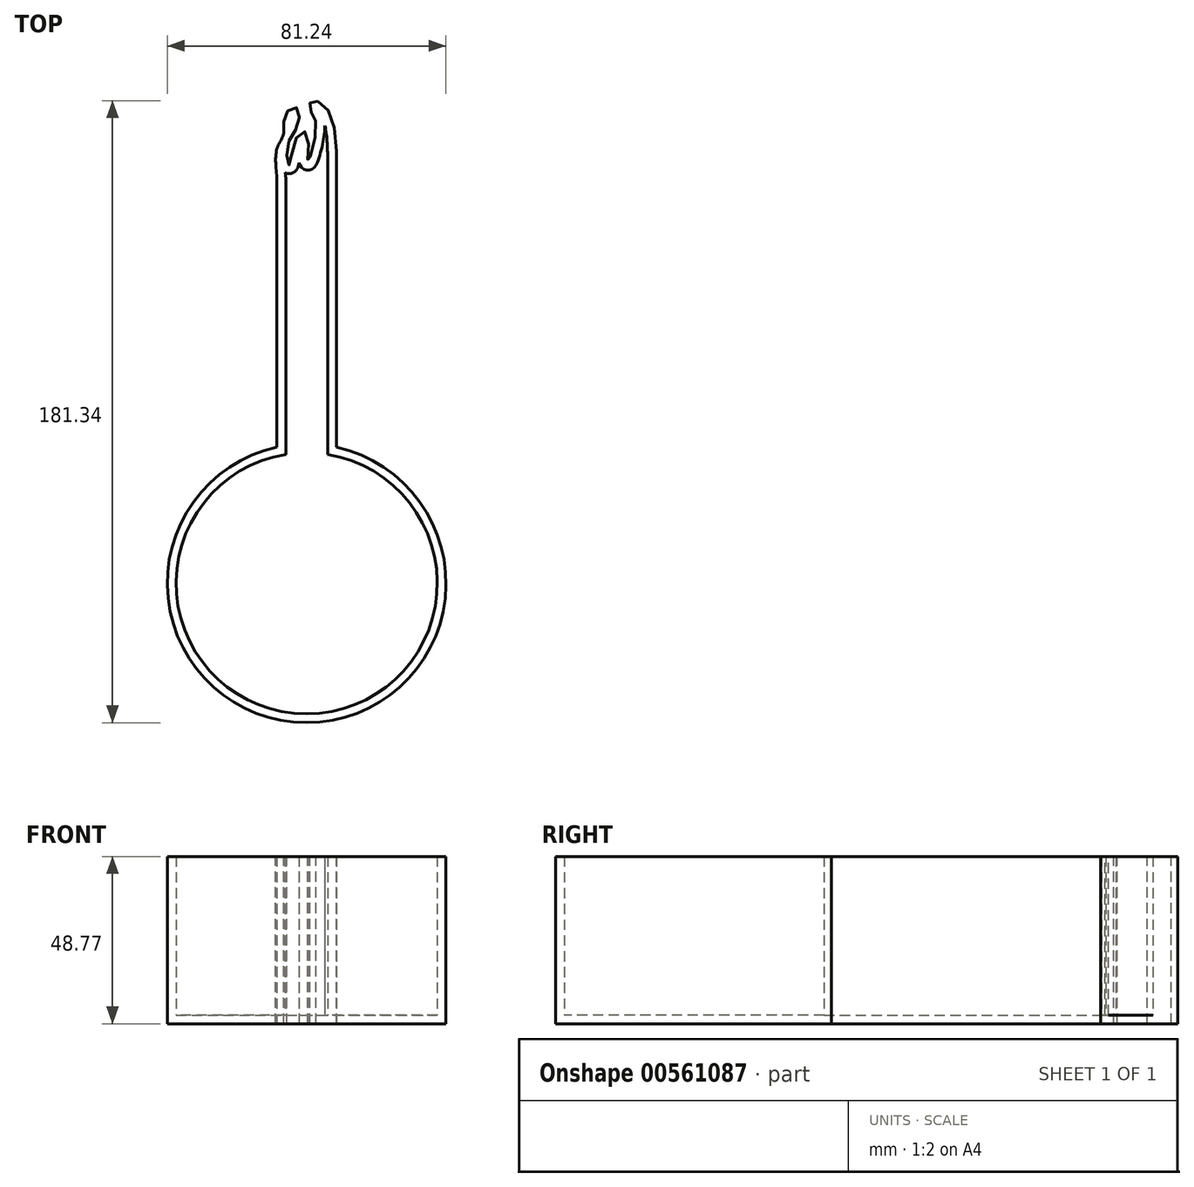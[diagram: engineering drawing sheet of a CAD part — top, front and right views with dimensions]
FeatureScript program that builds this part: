
annotation { "Feature Type Name" : "Feature", "Feature Type Description" : "" }
export const myFeature = defineFeature(function(context is Context, id is Id, definition is map)
    precondition{}
    {
        {
            var Q0;
            Q0=qCreatedBy(makeId("Top.planeOp"),FACE);
            var sketch = newSketch(context, id + "F0", { "sketchPlane" : qUnion([Q0])});
            skArc(sketch, "E0", {"start": v(-34.63, 33.43) * mm, "mid": v(-25.99, -46.89) * mm, "end": v(-17.34, 33.43) * mm});
            skLineSegment(sketch, "E1.bottom", {"start": v(-34.63, 33.43) * mm, "end": v(-17.34, 33.43) * mm});
            skLineSegment(sketch, "E1.top", {"start": v(-34.63, 112) * mm, "end": v(-17.34, 112) * mm});
            skLineSegment(sketch, "E1.left", {"start": v(-34.63, 33.43) * mm, "end": v(-34.63, 112) * mm});
            skLineSegment(sketch, "E1.right", {"start": v(-17.34, 33.43) * mm, "end": v(-17.34, 112) * mm});
            skFitSpline(sketch, "E2", {"points": [v(-34.63, 112) * mm, v(-34.63, 120.42) * mm, v(-32.69, 125.02) * mm, v(-32.22, 130.42) * mm, v(-28.93, 132.41) * mm, v(-28.59, 127.24) * mm, v(-31.67, 121.02) * mm, v(-31.08, 115.7) * mm, v(-28.6, 124.28) * mm, v(-25.9, 124.81) * mm, v(-25.64, 116.78) * mm, v(-23.2, 126.88) * mm, v(-24.75, 131.36) * mm, v(-24.65, 134.22) * mm, v(-20.16, 132.3) * mm, v(-17.34, 112) * mm], "startDerivative": vector(-13.4, 120.95) * mm, "endDerivative": vector(-2.18, -208.3) * mm});
            skFitSpline(sketch, "E3", {"points": [v(-32.69, 125.02) * mm, v(-34.63, 125.02) * mm], "startDerivative": vector(-1.94, 0) * mm, "endDerivative": vector(-1.94, 0) * mm});
            skPoint(sketch, "E4", {"position": v(-43.89, -14.02) * mm});
            skPoint(sketch, "E5", {"position": v(-22.18, -27.52) * mm});
            skPoint(sketch, "E6", {"position": v(-15.41, 9.1) * mm});
            skPoint(sketch, "E7", {"position": v(-33.5, 9.1) * mm});
            skPoint(sketch, "E8", {"position": v(-6.83, -14.02) * mm});
            skPoint(sketch, "E9", {"position": v(-43.89, -6.27) * mm});
            skPoint(sketch, "E10", {"position": v(-43.89, 0) * mm});
            skSolve(sketch);
        }
        {
            var Q0;
            {var subQ0=sQuery(id+"F0.wireOp",EDGE,"E1.top");Q0=makeQuery(id+"F0.imprint","IMPRINT",FACE,{"disambiguationData":[TD([[makeQuery(id+"F0.imprint","IMPRINT",EDGE,{"derivedFrom":subQ0}),1.0]])]});}
            var Q1;
            Q1=makeQuery(id+"F0.imprint","IMPRINT",FACE,{"disambiguationData":[TD([[makeQuery(id+"F0.imprint","IMPRINT",EDGE,{"derivedFrom":sQuery(id+"F0.wireOp",EDGE,"E1.bottom")}),1.0]])]});
            var Q2;
            Q2=makeQuery(id+"F0.imprint","IMPRINT",FACE,{"disambiguationData":[TD([[makeQuery(id+"F0.imprint","IMPRINT",EDGE,{"derivedFrom":sQuery(id+"F0.wireOp",EDGE,"E0")}),1.0]])]});
            extrude(context, id + "F1", {"entities" : qUnion([Q0, Q1, Q2]), "depth" : 48.77 * mm, "offsetDistance" : 25.4 * mm});
        }
        {
            var Q0;
            Q0=makeQuery(id+"F1.opExtrude","CAP_FACE",FACE,{"disambiguationData":[OSD([sQuery(id+"F0.wireOp",EDGE,"E0"),sQuery(id+"F0.wireOp",EDGE,"E1.left"),sQuery(id+"F0.wireOp",EDGE,"E1.right"),sQuery(id+"F0.wireOp",EDGE,"E2")])],"isStart":false});
            shell(context, id + "F2", {"entities" : qUnion([Q0]), "thickness" : 2.54 * mm});
        }
    });
